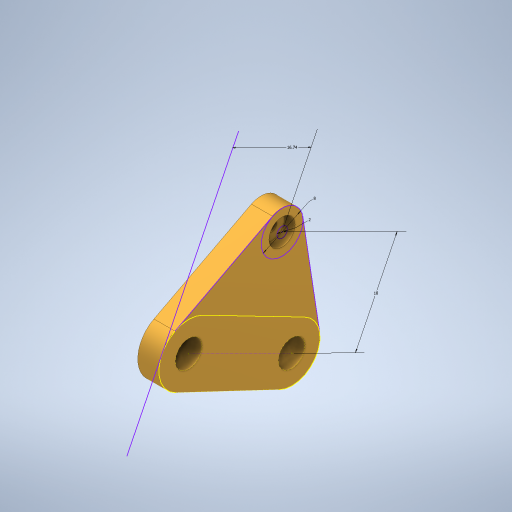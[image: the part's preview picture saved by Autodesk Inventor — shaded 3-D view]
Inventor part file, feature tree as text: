
AUTODESK INVENTOR PART (.ipt)
format: ipt  version: 2023 (Build 270158000, 158)  size: 295,936 bytes
history: native  units: in
note: dims shown in document units (in); Inventor stores cm internally (conversion verified against a paired STEP export)
features: extrude x3, sketch x3, projected_geometry x1
ambient origin geometry x8: Origin, YZ Plane, XZ Plane, XY Plane, X Axis, Y Axis, Z Axis, Center Point
bodies: Solid1 (feature_tree)
feature tree (7):
  extrude  "Extrusion1"  Depth=0.4523in
  extrude  "Extrusion2"  Depth=0.2118in
  extrude  "Extrusion3"  Depth=0.1575in TaperAngle=0.0deg
  sketch  "Sketch1"  dims[d0=0.2008in d1=0.2008in d3=0.4523in]
  sketch  "Sketch2"  dims[d4=0.2118in d5=0.8586in]
  projected_geometry  "Projected Loop1"
  sketch  "Sketch3"  dims[d6=0.8656in d7=0.1575in d8=0.0in d11=0.0787in d12=0.315in d13=0.1575in d14=0.0in d15=0.1969in d16=0.0787in d17=0.0in d18=0.6591in d19=0.7087in]
